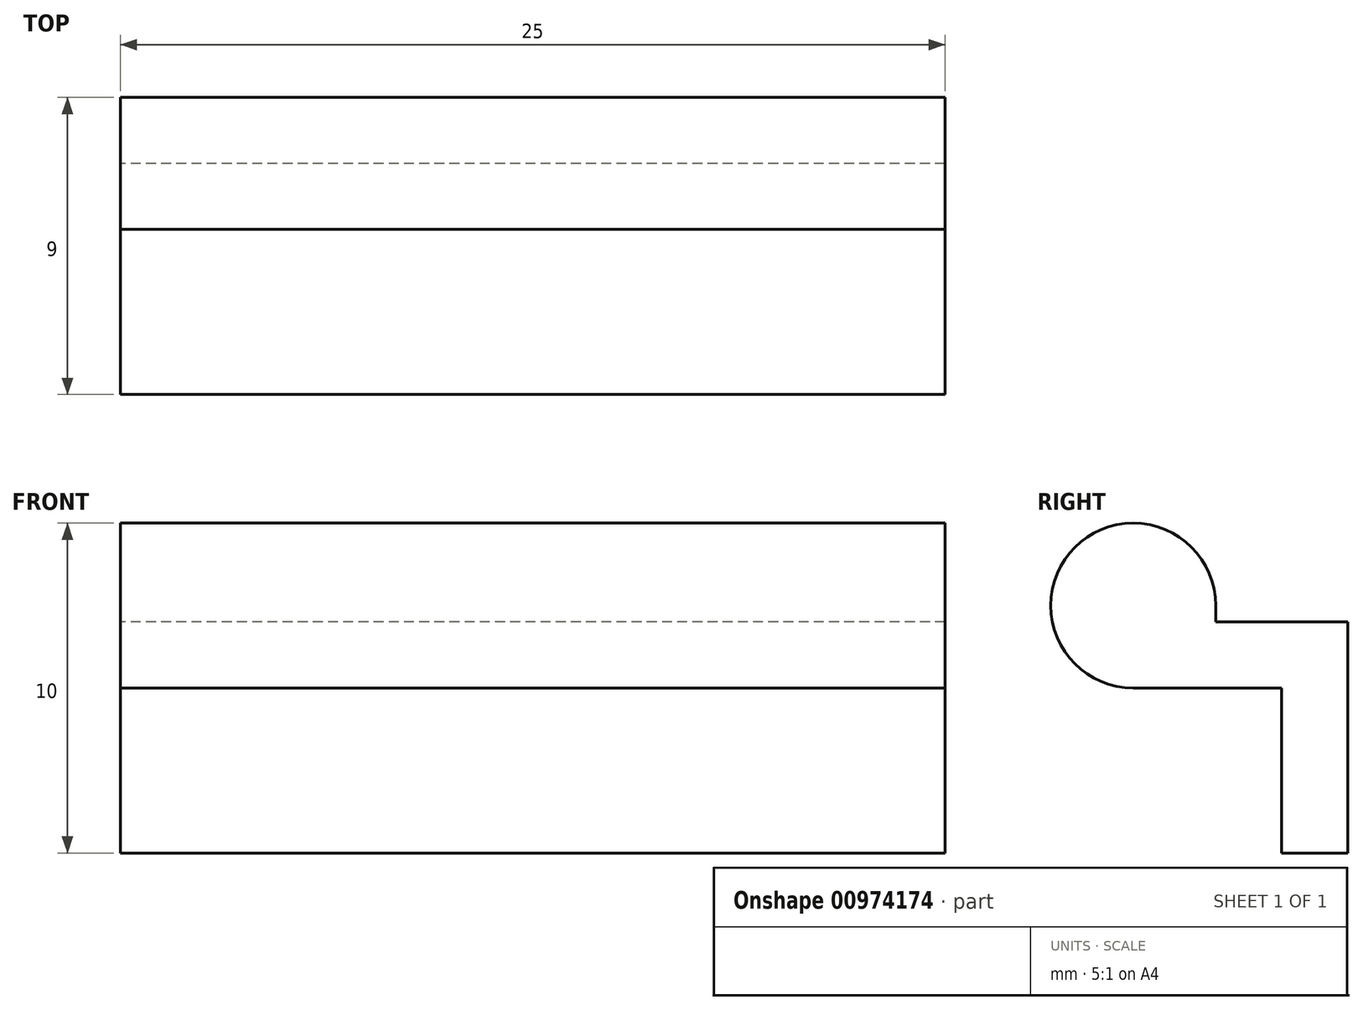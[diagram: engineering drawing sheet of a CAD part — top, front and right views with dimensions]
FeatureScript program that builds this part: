
annotation { "Feature Type Name" : "Feature", "Feature Type Description" : "" }
export const myFeature = defineFeature(function(context is Context, id is Id, definition is map)
    precondition{}
    {
        {
            var Q0;
            Q0=qCreatedBy(makeId("Right.planeOp"),FACE);
            var sketch = newSketch(context, id + "F0", { "sketchPlane" : qUnion([Q0])});
            skArc(sketch, "E0", {"start": v(2.5, 0) * mm, "mid": v(-1.77, 1.77) * mm, "end": v(0, -2.5) * mm});
            skLineSegment(sketch, "E1", {"start": v(0, -2.5) * mm, "end": v(4.5, -2.5) * mm});
            skLineSegment(sketch, "E2", {"start": v(4.5, -2.5) * mm, "end": v(4.5, -7.5) * mm});
            skLineSegment(sketch, "E3", {"start": v(4.5, -7.5) * mm, "end": v(6.5, -7.5) * mm});
            skLineSegment(sketch, "E4", {"start": v(6.5, -7.5) * mm, "end": v(6.5, -0.5) * mm});
            skLineSegment(sketch, "E5", {"start": v(6.5, -0.5) * mm, "end": v(2.5, -0.5) * mm});
            skLineSegment(sketch, "E6", {"start": v(2.5, 0) * mm, "end": v(2.5, -0.5) * mm});
            skSolve(sketch);
        }
        {
            var Q0;
            Q0 = qSketchRegion(id + "F0", true);
            extrude(context, id + "F1", {"entities" : qUnion([Q0]), "depth" : 25 * mm, "offsetDistance" : 25 * mm});
        }
    });
